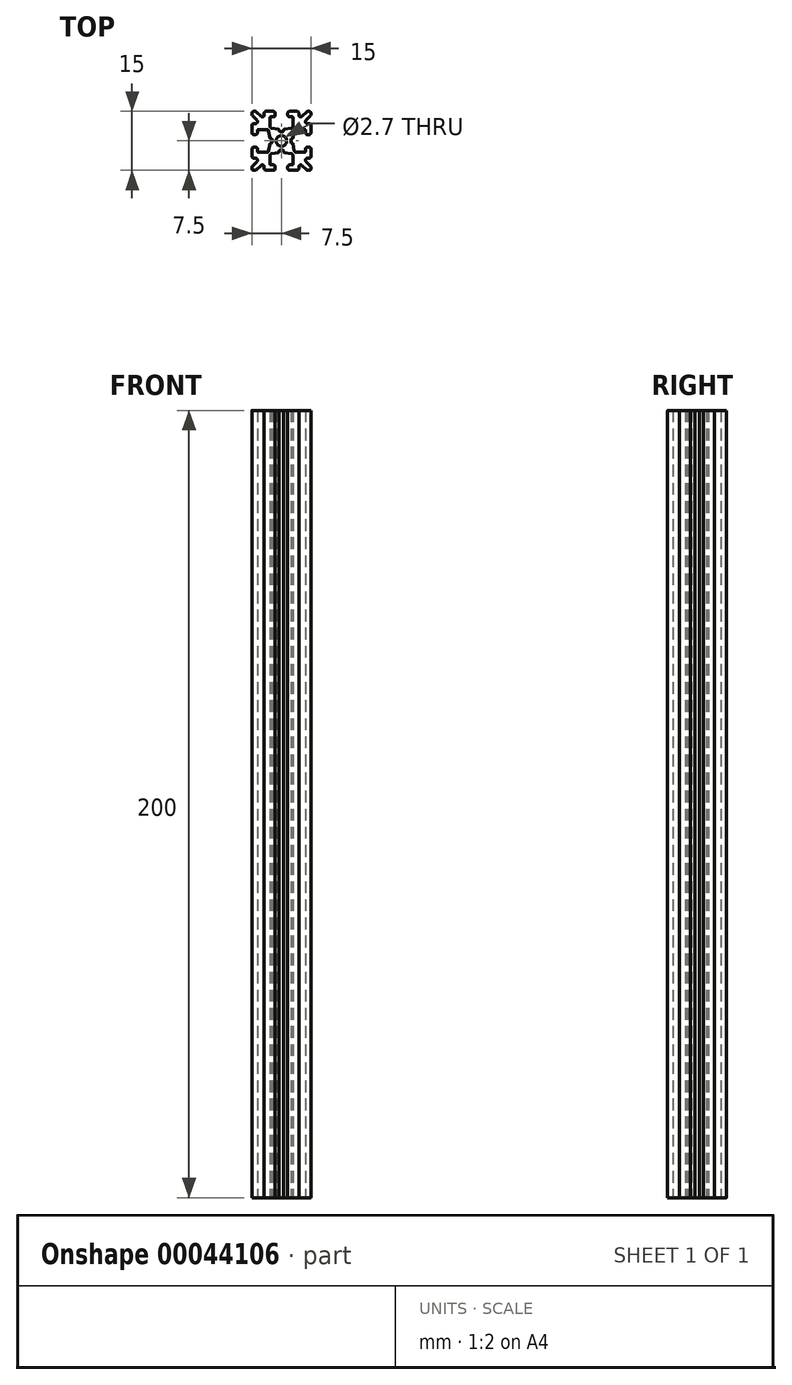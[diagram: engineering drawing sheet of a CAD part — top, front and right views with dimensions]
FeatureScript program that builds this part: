
annotation { "Feature Type Name" : "Feature", "Feature Type Description" : "" }
export const myFeature = defineFeature(function(context is Context, id is Id, definition is map)
    precondition{}
    {
        {
            var Q0;
            Q0=qCreatedBy(makeId("Top.planeOp"),FACE);
            var sketch = newSketch(context, id + "F0", { "sketchPlane" : qUnion([Q0])});
            skLineSegment(sketch, "E0", {"start": v(0, 0) * mm, "end": v(-7.5, -7.5) * mm, "construction": true});
            skArc(sketch, "E1", {"start": v(-1.35, 0) * mm, "mid": v(-1.25, -0.52) * mm, "end": v(-0.95, -0.95) * mm});
            skLineSegment(sketch, "E2", {"start": v(-7.5, -7) * mm, "end": v(-7.5, -6.72) * mm});
            skLineSegment(sketch, "E3", {"start": v(-7.35, -6.36) * mm, "end": v(-6.25, -5.26) * mm});
            skLineSegment(sketch, "E4", {"start": v(-6.6, -4.4) * mm, "end": v(-7, -4.4) * mm});
            skLineSegment(sketch, "E5", {"start": v(-7.5, -3.9) * mm, "end": v(-7.5, -2.1) * mm});
            skLineSegment(sketch, "E6", {"start": v(-7, -1.6) * mm, "end": v(-6.6, -1.6) * mm});
            skLineSegment(sketch, "E7", {"start": v(-6.1, -2.1) * mm, "end": v(-6.1, -2.7) * mm});
            skLineSegment(sketch, "E8", {"start": v(-5.9, -2.9) * mm, "end": v(-3.74, -2.9) * mm});
            skLineSegment(sketch, "E9", {"start": v(-3.25, -2.49) * mm, "end": v(-2.93, -0.73) * mm});
            skLineSegment(sketch, "E10", {"start": v(-2.73, -0.57) * mm, "end": v(-2.6, -0.57) * mm});
            skLineSegment(sketch, "E11", {"start": v(-2.4, -0.37) * mm, "end": v(-2.4, 0) * mm});
            skLineSegment(sketch, "E12", {"start": v(-2.4, 0) * mm, "end": v(-1.35, 0) * mm, "construction": true});
            skPoint(sketch, "E13.visualSharp", {"position": v(-5.4, -4.4) * mm});
            skArc(sketch, "E13.filletArc", {"start": v(-6.25, -5.26) * mm, "mid": v(-6.14, -4.71) * mm, "end": v(-6.6, -4.4) * mm});
            skPoint(sketch, "E14.visualSharp", {"position": v(-6.1, -2.9) * mm});
            skArc(sketch, "E14.filletArc", {"start": v(-6.1, -2.7) * mm, "mid": v(-6.04, -2.84) * mm, "end": v(-5.9, -2.9) * mm});
            skPoint(sketch, "E15.visualSharp", {"position": v(-6.1, -1.6) * mm});
            skArc(sketch, "E15.filletArc", {"start": v(-6.1, -2.1) * mm, "mid": v(-6.25, -1.75) * mm, "end": v(-6.6, -1.6) * mm});
            skPoint(sketch, "E16.visualSharp", {"position": v(-7.5, -1.6) * mm});
            skArc(sketch, "E16.filletArc", {"start": v(-7, -1.6) * mm, "mid": v(-7.35, -1.75) * mm, "end": v(-7.5, -2.1) * mm});
            skPoint(sketch, "E17.visualSharp", {"position": v(-7.5, -4.4) * mm});
            skArc(sketch, "E17.filletArc", {"start": v(-7.5, -3.9) * mm, "mid": v(-7.35, -4.26) * mm, "end": v(-7, -4.4) * mm});
            skPoint(sketch, "E18.visualSharp", {"position": v(-7.5, -6.51) * mm});
            skArc(sketch, "E18.filletArc", {"start": v(-7.35, -6.36) * mm, "mid": v(-7.46, -6.53) * mm, "end": v(-7.5, -6.72) * mm});
            skPoint(sketch, "E19.visualSharp", {"position": v(-3.32, -2.9) * mm});
            skArc(sketch, "E19.filletArc", {"start": v(-3.74, -2.9) * mm, "mid": v(-3.42, -2.78) * mm, "end": v(-3.25, -2.49) * mm});
            skPoint(sketch, "E20.visualSharp", {"position": v(-2.9, -0.57) * mm});
            skArc(sketch, "E20.filletArc", {"start": v(-2.73, -0.57) * mm, "mid": v(-2.86, -0.62) * mm, "end": v(-2.93, -0.73) * mm});
            skPoint(sketch, "E21.visualSharp", {"position": v(-2.4, -0.57) * mm});
            skArc(sketch, "E21.filletArc", {"start": v(-2.6, -0.57) * mm, "mid": v(-2.46, -0.51) * mm, "end": v(-2.4, -0.37) * mm});
            skLineSegment(sketch, "E22.0.MirrorCS", {"start": v(0, -2.4) * mm, "end": v(0, -1.35) * mm, "construction": true});
            skPoint(sketch, "E22.1.MirrorP", {"position": v(-4.4, -7.5) * mm});
            skArc(sketch, "E22.2.MirrorCS", {"start": v(-6.36, -7.35) * mm, "mid": v(-6.53, -7.46) * mm, "end": v(-6.72, -7.5) * mm});
            skPoint(sketch, "E22.3.MirrorP", {"position": v(-1.6, -7.5) * mm});
            skArc(sketch, "E22.4.MirrorCS", {"start": v(-1.6, -7) * mm, "mid": v(-1.75, -7.35) * mm, "end": v(-2.1, -7.5) * mm});
            skArc(sketch, "E22.5.MirrorCS", {"start": v(-0.57, -2.73) * mm, "mid": v(-0.62, -2.86) * mm, "end": v(-0.73, -2.93) * mm});
            skPoint(sketch, "E22.6.MirrorP", {"position": v(-1.6, -6.1) * mm});
            skLineSegment(sketch, "E22.7.MirrorCS", {"start": v(-3.9, -7.5) * mm, "end": v(-2.1, -7.5) * mm});
            skArc(sketch, "E22.8.MirrorCS", {"start": v(-5.26, -6.25) * mm, "mid": v(-4.71, -6.14) * mm, "end": v(-4.4, -6.6) * mm});
            skPoint(sketch, "E22.9.MirrorP", {"position": v(-0.57, -2.4) * mm});
            skPoint(sketch, "E22.10.MirrorP", {"position": v(-4.4, -5.4) * mm});
            skArc(sketch, "E22.11.MirrorCS", {"start": v(-2.7, -6.1) * mm, "mid": v(-2.84, -6.04) * mm, "end": v(-2.9, -5.9) * mm});
            skPoint(sketch, "E22.12.MirrorP", {"position": v(-0.57, -2.9) * mm});
            skLineSegment(sketch, "E22.13.MirrorCS", {"start": v(-7, -7.5) * mm, "end": v(-6.72, -7.5) * mm});
            skLineSegment(sketch, "E22.14.MirrorCS", {"start": v(-1.6, -7) * mm, "end": v(-1.6, -6.6) * mm});
            skLineSegment(sketch, "E22.15.MirrorCS", {"start": v(-6.36, -7.35) * mm, "end": v(-5.26, -6.25) * mm});
            skArc(sketch, "E22.16.MirrorCS", {"start": v(-2.1, -6.1) * mm, "mid": v(-1.75, -6.25) * mm, "end": v(-1.6, -6.6) * mm});
            skLineSegment(sketch, "E22.17.MirrorCS", {"start": v(-4.4, -6.6) * mm, "end": v(-4.4, -7) * mm});
            skArc(sketch, "E22.18.MirrorCS", {"start": v(-2.9, -3.74) * mm, "mid": v(-2.78, -3.42) * mm, "end": v(-2.49, -3.25) * mm});
            skLineSegment(sketch, "E22.19.MirrorCS", {"start": v(-2.9, -5.9) * mm, "end": v(-2.9, -3.74) * mm});
            skLineSegment(sketch, "E22.20.MirrorCS", {"start": v(-2.1, -6.1) * mm, "end": v(-2.7, -6.1) * mm});
            skArc(sketch, "E22.21.MirrorCS", {"start": v(-0.57, -2.6) * mm, "mid": v(-0.51, -2.46) * mm, "end": v(-0.37, -2.4) * mm});
            skLineSegment(sketch, "E22.22.MirrorCS", {"start": v(-0.37, -2.4) * mm, "end": v(0, -2.4) * mm});
            skPoint(sketch, "E22.23.MirrorP", {"position": v(-6.51, -7.5) * mm});
            skPoint(sketch, "E22.24.MirrorP", {"position": v(-2.9, -6.1) * mm});
            skLineSegment(sketch, "E22.25.MirrorCS", {"start": v(-2.49, -3.25) * mm, "end": v(-0.73, -2.93) * mm});
            skLineSegment(sketch, "E22.26.MirrorCS", {"start": v(-0.57, -2.73) * mm, "end": v(-0.57, -2.6) * mm});
            skArc(sketch, "E22.27.MirrorCS", {"start": v(0, -1.35) * mm, "mid": v(-0.52, -1.25) * mm, "end": v(-0.95, -0.95) * mm});
            skArc(sketch, "E22.28.MirrorCS", {"start": v(-3.9, -7.5) * mm, "mid": v(-4.26, -7.35) * mm, "end": v(-4.4, -7) * mm});
            skPoint(sketch, "E22.29.MirrorP", {"position": v(-2.9, -3.32) * mm});
            skPoint(sketch, "E23.visualSharp", {"position": v(-7.5, -7.5) * mm});
            skArc(sketch, "E23.filletArc", {"start": v(-7.5, -7) * mm, "mid": v(-7.35, -7.35) * mm, "end": v(-7, -7.5) * mm});
            skLineSegment(sketch, "E24.0.MirrorCS", {"start": v(0, 2.4) * mm, "end": v(0, 1.35) * mm, "construction": true});
            skLineSegment(sketch, "E24.1.MirrorCS", {"start": v(-2.1, 6.1) * mm, "end": v(-2.7, 6.1) * mm});
            skLineSegment(sketch, "E24.2.MirrorCS", {"start": v(-7.5, 3.9) * mm, "end": v(-7.5, 2.1) * mm});
            skLineSegment(sketch, "E24.3.MirrorCS", {"start": v(-7, 1.6) * mm, "end": v(-6.6, 1.6) * mm});
            skArc(sketch, "E24.4.MirrorCS", {"start": v(-6.1, 2.1) * mm, "mid": v(-6.25, 1.75) * mm, "end": v(-6.6, 1.6) * mm});
            skPoint(sketch, "E24.5.MirrorP", {"position": v(-3.32, 2.9) * mm});
            skPoint(sketch, "E24.6.MirrorP", {"position": v(-0.57, 2.9) * mm});
            skArc(sketch, "E24.7.MirrorCS", {"start": v(-0.57, 2.6) * mm, "mid": v(-0.51, 2.46) * mm, "end": v(-0.37, 2.4) * mm});
            skArc(sketch, "E24.8.MirrorCS", {"start": v(-2.6, 0.57) * mm, "mid": v(-2.46, 0.51) * mm, "end": v(-2.4, 0.37) * mm});
            skLineSegment(sketch, "E24.9.MirrorCS", {"start": v(-0.37, 2.4) * mm, "end": v(0, 2.4) * mm});
            skArc(sketch, "E24.10.MirrorCS", {"start": v(-6.1, 2.7) * mm, "mid": v(-6.04, 2.84) * mm, "end": v(-5.9, 2.9) * mm});
            skPoint(sketch, "E24.11.MirrorP", {"position": v(-4.4, 5.4) * mm});
            skLineSegment(sketch, "E24.12.MirrorCS", {"start": v(-2.9, 5.9) * mm, "end": v(-2.9, 3.74) * mm});
            skLineSegment(sketch, "E24.13.MirrorCS", {"start": v(-7.35, 6.36) * mm, "end": v(-6.25, 5.26) * mm});
            skPoint(sketch, "E24.14.MirrorP", {"position": v(-7.5, 6.51) * mm});
            skArc(sketch, "E24.15.MirrorCS", {"start": v(-3.74, 2.9) * mm, "mid": v(-3.42, 2.78) * mm, "end": v(-3.25, 2.49) * mm});
            skArc(sketch, "E24.16.MirrorCS", {"start": v(-2.1, 6.1) * mm, "mid": v(-1.75, 6.25) * mm, "end": v(-1.6, 6.6) * mm});
            skArc(sketch, "E24.17.MirrorCS", {"start": v(-7, 1.6) * mm, "mid": v(-7.35, 1.75) * mm, "end": v(-7.5, 2.1) * mm});
            skPoint(sketch, "E24.18.MirrorP", {"position": v(-1.6, 6.1) * mm});
            skPoint(sketch, "E24.19.MirrorP", {"position": v(-7.5, 4.4) * mm});
            skLineSegment(sketch, "E24.20.MirrorCS", {"start": v(-4.4, 6.6) * mm, "end": v(-4.4, 7) * mm});
            skArc(sketch, "E24.21.MirrorCS", {"start": v(-7.5, 3.9) * mm, "mid": v(-7.35, 4.26) * mm, "end": v(-7, 4.4) * mm});
            skPoint(sketch, "E24.22.MirrorP", {"position": v(-0.57, 2.4) * mm});
            skLineSegment(sketch, "E24.23.MirrorCS", {"start": v(-5.9, 2.9) * mm, "end": v(-3.74, 2.9) * mm});
            skArc(sketch, "E24.24.MirrorCS", {"start": v(-2.9, 3.74) * mm, "mid": v(-2.78, 3.42) * mm, "end": v(-2.49, 3.25) * mm});
            skArc(sketch, "E24.25.MirrorCS", {"start": v(-7.35, 6.36) * mm, "mid": v(-7.46, 6.53) * mm, "end": v(-7.5, 6.72) * mm});
            skPoint(sketch, "E24.26.MirrorP", {"position": v(-6.1, 2.9) * mm});
            skPoint(sketch, "E24.27.MirrorP", {"position": v(-4.4, 7.5) * mm});
            skArc(sketch, "E24.28.MirrorCS", {"start": v(-5.26, 6.25) * mm, "mid": v(-4.71, 6.14) * mm, "end": v(-4.4, 6.6) * mm});
            skArc(sketch, "E24.29.MirrorCS", {"start": v(-7.5, 7) * mm, "mid": v(-7.35, 7.35) * mm, "end": v(-7, 7.5) * mm});
            skPoint(sketch, "E24.30.MirrorP", {"position": v(-6.1, 1.6) * mm});
            skPoint(sketch, "E24.31.MirrorP", {"position": v(-2.9, 3.32) * mm});
            skPoint(sketch, "E24.32.MirrorP", {"position": v(-1.6, 7.5) * mm});
            skPoint(sketch, "E24.33.MirrorP", {"position": v(-2.9, 6.1) * mm});
            skLineSegment(sketch, "E24.34.MirrorCS", {"start": v(-3.9, 7.5) * mm, "end": v(-2.1, 7.5) * mm});
            skLineSegment(sketch, "E24.35.MirrorCS", {"start": v(-7, 7.5) * mm, "end": v(-6.72, 7.5) * mm});
            skArc(sketch, "E24.36.MirrorCS", {"start": v(-3.9, 7.5) * mm, "mid": v(-4.26, 7.35) * mm, "end": v(-4.4, 7) * mm});
            skPoint(sketch, "E24.37.MirrorP", {"position": v(-7.5, 7.5) * mm});
            skLineSegment(sketch, "E24.38.MirrorCS", {"start": v(-1.6, 7) * mm, "end": v(-1.6, 6.6) * mm});
            skLineSegment(sketch, "E24.39.MirrorCS", {"start": v(-6.36, 7.35) * mm, "end": v(-5.26, 6.25) * mm});
            skPoint(sketch, "E24.40.MirrorP", {"position": v(-7.5, 1.6) * mm});
            skArc(sketch, "E24.41.MirrorCS", {"start": v(-2.7, 6.1) * mm, "mid": v(-2.84, 6.04) * mm, "end": v(-2.9, 5.9) * mm});
            skArc(sketch, "E24.42.MirrorCS", {"start": v(-6.36, 7.35) * mm, "mid": v(-6.53, 7.46) * mm, "end": v(-6.72, 7.5) * mm});
            skLineSegment(sketch, "E24.43.MirrorCS", {"start": v(-2.49, 3.25) * mm, "end": v(-0.73, 2.93) * mm});
            skPoint(sketch, "E24.44.MirrorP", {"position": v(-2.9, 0.57) * mm});
            skLineSegment(sketch, "E24.45.MirrorCS", {"start": v(-6.6, 4.4) * mm, "end": v(-7, 4.4) * mm});
            skArc(sketch, "E24.46.MirrorCS", {"start": v(-1.6, 7) * mm, "mid": v(-1.75, 7.35) * mm, "end": v(-2.1, 7.5) * mm});
            skArc(sketch, "E24.47.MirrorCS", {"start": v(-2.73, 0.57) * mm, "mid": v(-2.86, 0.62) * mm, "end": v(-2.93, 0.73) * mm});
            skArc(sketch, "E24.48.MirrorCS", {"start": v(-6.25, 5.26) * mm, "mid": v(-6.14, 4.71) * mm, "end": v(-6.6, 4.4) * mm});
            skLineSegment(sketch, "E24.49.MirrorCS", {"start": v(-0.57, 2.73) * mm, "end": v(-0.57, 2.6) * mm});
            skLineSegment(sketch, "E24.50.MirrorCS", {"start": v(-2.73, 0.57) * mm, "end": v(-2.6, 0.57) * mm});
            skArc(sketch, "E24.51.MirrorCS", {"start": v(-1.35, 0) * mm, "mid": v(-1.25, 0.52) * mm, "end": v(-0.95, 0.95) * mm});
            skPoint(sketch, "E24.52.MirrorP", {"position": v(-2.4, 0.57) * mm});
            skPoint(sketch, "E24.53.MirrorP", {"position": v(-5.4, 4.4) * mm});
            skLineSegment(sketch, "E24.54.MirrorCS", {"start": v(-2.4, 0.37) * mm, "end": v(-2.4, 0) * mm});
            skArc(sketch, "E24.55.MirrorCS", {"start": v(0, 1.35) * mm, "mid": v(-0.52, 1.25) * mm, "end": v(-0.95, 0.95) * mm});
            skLineSegment(sketch, "E24.56.MirrorCS", {"start": v(-3.25, 2.49) * mm, "end": v(-2.93, 0.73) * mm});
            skLineSegment(sketch, "E24.57.MirrorCS", {"start": v(-6.1, 2.1) * mm, "end": v(-6.1, 2.7) * mm});
            skLineSegment(sketch, "E24.58.MirrorCS", {"start": v(-7.5, 7) * mm, "end": v(-7.5, 6.72) * mm});
            skArc(sketch, "E24.59.MirrorCS", {"start": v(-0.57, 2.73) * mm, "mid": v(-0.62, 2.86) * mm, "end": v(-0.73, 2.93) * mm});
            skPoint(sketch, "E24.60.MirrorP", {"position": v(-6.51, 7.5) * mm});
            skLineSegment(sketch, "E25.0.MirrorCS", {"start": v(7, -7.5) * mm, "end": v(6.72, -7.5) * mm});
            skLineSegment(sketch, "E25.1.MirrorCS", {"start": v(0.57, 2.73) * mm, "end": v(0.57, 2.6) * mm});
            skLineSegment(sketch, "E25.2.MirrorCS", {"start": v(0.37, 2.4) * mm, "end": v(0, 2.4) * mm});
            skLineSegment(sketch, "E25.3.MirrorCS", {"start": v(7, 7.5) * mm, "end": v(6.72, 7.5) * mm});
            skLineSegment(sketch, "E25.4.MirrorCS", {"start": v(1.6, -7) * mm, "end": v(1.6, -6.6) * mm});
            skLineSegment(sketch, "E25.5.MirrorCS", {"start": v(2.73, 0.57) * mm, "end": v(2.6, 0.57) * mm});
            skLineSegment(sketch, "E25.6.MirrorCS", {"start": v(7, 1.6) * mm, "end": v(6.6, 1.6) * mm});
            skLineSegment(sketch, "E25.7.MirrorCS", {"start": v(5.9, 2.9) * mm, "end": v(3.74, 2.9) * mm});
            skLineSegment(sketch, "E25.8.MirrorCS", {"start": v(7.35, 6.36) * mm, "end": v(6.25, 5.26) * mm});
            skArc(sketch, "E25.9.MirrorCS", {"start": v(2.7, -6.1) * mm, "mid": v(2.84, -6.04) * mm, "end": v(2.9, -5.9) * mm});
            skArc(sketch, "E25.10.MirrorCS", {"start": v(2.9, 3.74) * mm, "mid": v(2.78, 3.42) * mm, "end": v(2.49, 3.25) * mm});
            skPoint(sketch, "E25.11.MirrorP", {"position": v(1.6, -7.5) * mm});
            skPoint(sketch, "E25.12.MirrorP", {"position": v(6.1, -1.6) * mm});
            skPoint(sketch, "E25.13.MirrorP", {"position": v(2.9, 3.32) * mm});
            skPoint(sketch, "E25.14.MirrorP", {"position": v(7.5, -1.6) * mm});
            skArc(sketch, "E25.15.MirrorCS", {"start": v(1.6, 7) * mm, "mid": v(1.75, 7.35) * mm, "end": v(2.1, 7.5) * mm});
            skLineSegment(sketch, "E25.16.MirrorCS", {"start": v(6.1, -2.1) * mm, "end": v(6.1, -2.7) * mm});
            skLineSegment(sketch, "E25.17.MirrorCS", {"start": v(2.4, 0.37) * mm, "end": v(2.4, 0) * mm});
            skArc(sketch, "E25.18.MirrorCS", {"start": v(7, -1.6) * mm, "mid": v(7.35, -1.75) * mm, "end": v(7.5, -2.1) * mm});
            skArc(sketch, "E25.19.MirrorCS", {"start": v(7.5, 7) * mm, "mid": v(7.35, 7.35) * mm, "end": v(7, 7.5) * mm});
            skArc(sketch, "E25.20.MirrorCS", {"start": v(2.1, -6.1) * mm, "mid": v(1.75, -6.25) * mm, "end": v(1.6, -6.6) * mm});
            skArc(sketch, "E25.21.MirrorCS", {"start": v(6.1, 2.1) * mm, "mid": v(6.25, 1.75) * mm, "end": v(6.6, 1.6) * mm});
            skLineSegment(sketch, "E25.22.MirrorCS", {"start": v(4.4, 6.6) * mm, "end": v(4.4, 7) * mm});
            skLineSegment(sketch, "E25.23.MirrorCS", {"start": v(6.6, 4.4) * mm, "end": v(7, 4.4) * mm});
            skArc(sketch, "E25.24.MirrorCS", {"start": v(7, 1.6) * mm, "mid": v(7.35, 1.75) * mm, "end": v(7.5, 2.1) * mm});
            skArc(sketch, "E25.25.MirrorCS", {"start": v(0, -1.35) * mm, "mid": v(0.52, -1.25) * mm, "end": v(0.95, -0.95) * mm});
            skLineSegment(sketch, "E25.26.MirrorCS", {"start": v(3.9, -7.5) * mm, "end": v(2.1, -7.5) * mm});
            skLineSegment(sketch, "E25.27.MirrorCS", {"start": v(2.1, 6.1) * mm, "end": v(2.7, 6.1) * mm});
            skLineSegment(sketch, "E25.28.MirrorCS", {"start": v(2.73, -0.57) * mm, "end": v(2.6, -0.57) * mm});
            skLineSegment(sketch, "E25.29.MirrorCS", {"start": v(4.4, -6.6) * mm, "end": v(4.4, -7) * mm});
            skLineSegment(sketch, "E25.30.MirrorCS", {"start": v(3.9, 7.5) * mm, "end": v(2.1, 7.5) * mm});
            skArc(sketch, "E25.31.MirrorCS", {"start": v(0.57, -2.73) * mm, "mid": v(0.62, -2.86) * mm, "end": v(0.73, -2.93) * mm});
            skArc(sketch, "E25.32.MirrorCS", {"start": v(0.57, 2.6) * mm, "mid": v(0.51, 2.46) * mm, "end": v(0.37, 2.4) * mm});
            skPoint(sketch, "E25.33.MirrorP", {"position": v(6.51, -7.5) * mm});
            skArc(sketch, "E25.34.MirrorCS", {"start": v(3.9, -7.5) * mm, "mid": v(4.26, -7.35) * mm, "end": v(4.4, -7) * mm});
            skArc(sketch, "E25.35.MirrorCS", {"start": v(2.7, 6.1) * mm, "mid": v(2.84, 6.04) * mm, "end": v(2.9, 5.9) * mm});
            skPoint(sketch, "E25.36.MirrorP", {"position": v(0.57, -2.4) * mm});
            skPoint(sketch, "E25.37.MirrorP", {"position": v(0.57, 2.9) * mm});
            skLineSegment(sketch, "E25.38.MirrorCS", {"start": v(3.25, -2.49) * mm, "end": v(2.93, -0.73) * mm});
            skPoint(sketch, "E25.39.MirrorP", {"position": v(5.4, -4.4) * mm});
            skPoint(sketch, "E25.40.MirrorP", {"position": v(2.4, -0.57) * mm});
            skLineSegment(sketch, "E25.41.MirrorCS", {"start": v(7.5, -7) * mm, "end": v(7.5, -6.72) * mm});
            skArc(sketch, "E25.42.MirrorCS", {"start": v(7.35, 6.36) * mm, "mid": v(7.46, 6.53) * mm, "end": v(7.5, 6.72) * mm});
            skPoint(sketch, "E25.43.MirrorP", {"position": v(4.4, 7.5) * mm});
            skArc(sketch, "E25.44.MirrorCS", {"start": v(6.25, 5.26) * mm, "mid": v(6.14, 4.71) * mm, "end": v(6.6, 4.4) * mm});
            skPoint(sketch, "E25.45.MirrorP", {"position": v(6.1, -2.9) * mm});
            skPoint(sketch, "E25.46.MirrorP", {"position": v(4.4, -7.5) * mm});
            skArc(sketch, "E25.47.MirrorCS", {"start": v(6.1, 2.7) * mm, "mid": v(6.04, 2.84) * mm, "end": v(5.9, 2.9) * mm});
            skLineSegment(sketch, "E25.48.MirrorCS", {"start": v(2.1, -6.1) * mm, "end": v(2.7, -6.1) * mm});
            skArc(sketch, "E25.49.MirrorCS", {"start": v(2.73, -0.57) * mm, "mid": v(2.86, -0.62) * mm, "end": v(2.93, -0.73) * mm});
            skArc(sketch, "E25.50.MirrorCS", {"start": v(7.35, -6.36) * mm, "mid": v(7.46, -6.53) * mm, "end": v(7.5, -6.72) * mm});
            skLineSegment(sketch, "E25.51.MirrorCS", {"start": v(3.25, 2.49) * mm, "end": v(2.93, 0.73) * mm});
            skArc(sketch, "E25.52.MirrorCS", {"start": v(2.9, -3.74) * mm, "mid": v(2.78, -3.42) * mm, "end": v(2.49, -3.25) * mm});
            skArc(sketch, "E25.53.MirrorCS", {"start": v(2.6, 0.57) * mm, "mid": v(2.46, 0.51) * mm, "end": v(2.4, 0.37) * mm});
            skPoint(sketch, "E25.54.MirrorP", {"position": v(2.9, 0.57) * mm});
            skPoint(sketch, "E25.55.MirrorP", {"position": v(7.5, -6.51) * mm});
            skLineSegment(sketch, "E25.56.MirrorCS", {"start": v(2.49, 3.25) * mm, "end": v(0.73, 2.93) * mm});
            skArc(sketch, "E25.57.MirrorCS", {"start": v(1.6, -7) * mm, "mid": v(1.75, -7.35) * mm, "end": v(2.1, -7.5) * mm});
            skArc(sketch, "E25.58.MirrorCS", {"start": v(2.1, 6.1) * mm, "mid": v(1.75, 6.25) * mm, "end": v(1.6, 6.6) * mm});
            skLineSegment(sketch, "E25.59.MirrorCS", {"start": v(0.57, -2.73) * mm, "end": v(0.57, -2.6) * mm});
            skLineSegment(sketch, "E25.60.MirrorCS", {"start": v(2.4, -0.37) * mm, "end": v(2.4, 0) * mm});
            skArc(sketch, "E25.61.MirrorCS", {"start": v(7.5, -3.9) * mm, "mid": v(7.35, -4.26) * mm, "end": v(7, -4.4) * mm});
            skLineSegment(sketch, "E25.62.MirrorCS", {"start": v(5.9, -2.9) * mm, "end": v(3.74, -2.9) * mm});
            skLineSegment(sketch, "E25.63.MirrorCS", {"start": v(7.5, -3.9) * mm, "end": v(7.5, -2.1) * mm});
            skLineSegment(sketch, "E25.64.MirrorCS", {"start": v(7, -1.6) * mm, "end": v(6.6, -1.6) * mm});
            skArc(sketch, "E25.65.MirrorCS", {"start": v(1.35, 0) * mm, "mid": v(1.25, -0.52) * mm, "end": v(0.95, -0.95) * mm});
            skPoint(sketch, "E25.66.MirrorP", {"position": v(7.5, 1.6) * mm});
            skPoint(sketch, "E25.67.MirrorP", {"position": v(1.6, 6.1) * mm});
            skLineSegment(sketch, "E25.68.MirrorCS", {"start": v(6.36, -7.35) * mm, "end": v(5.26, -6.25) * mm});
            skPoint(sketch, "E25.69.MirrorP", {"position": v(2.4, 0.57) * mm});
            skPoint(sketch, "E25.70.MirrorP", {"position": v(6.1, 1.6) * mm});
            skPoint(sketch, "E25.71.MirrorP", {"position": v(3.32, -2.9) * mm});
            skPoint(sketch, "E25.72.MirrorP", {"position": v(0.57, -2.9) * mm});
            skPoint(sketch, "E25.73.MirrorP", {"position": v(7.5, 4.4) * mm});
            skArc(sketch, "E25.74.MirrorCS", {"start": v(5.26, -6.25) * mm, "mid": v(4.71, -6.14) * mm, "end": v(4.4, -6.6) * mm});
            skArc(sketch, "E25.75.MirrorCS", {"start": v(7.5, -7) * mm, "mid": v(7.35, -7.35) * mm, "end": v(7, -7.5) * mm});
            skLineSegment(sketch, "E25.76.MirrorCS", {"start": v(2.49, -3.25) * mm, "end": v(0.73, -2.93) * mm});
            skArc(sketch, "E25.77.MirrorCS", {"start": v(3.74, 2.9) * mm, "mid": v(3.42, 2.78) * mm, "end": v(3.25, 2.49) * mm});
            skArc(sketch, "E25.78.MirrorCS", {"start": v(6.36, -7.35) * mm, "mid": v(6.53, -7.46) * mm, "end": v(6.72, -7.5) * mm});
            skArc(sketch, "E25.79.MirrorCS", {"start": v(7.5, 3.9) * mm, "mid": v(7.35, 4.26) * mm, "end": v(7, 4.4) * mm});
            skArc(sketch, "E25.80.MirrorCS", {"start": v(2.73, 0.57) * mm, "mid": v(2.86, 0.62) * mm, "end": v(2.93, 0.73) * mm});
            skArc(sketch, "E25.81.MirrorCS", {"start": v(6.36, 7.35) * mm, "mid": v(6.53, 7.46) * mm, "end": v(6.72, 7.5) * mm});
            skPoint(sketch, "E25.82.MirrorP", {"position": v(4.4, -5.4) * mm});
            skPoint(sketch, "E25.83.MirrorP", {"position": v(6.51, 7.5) * mm});
            skPoint(sketch, "E25.84.MirrorP", {"position": v(2.9, -0.57) * mm});
            skLineSegment(sketch, "E25.85.MirrorCS", {"start": v(2.9, -5.9) * mm, "end": v(2.9, -3.74) * mm});
            skLineSegment(sketch, "E25.86.MirrorCS", {"start": v(6.1, 2.1) * mm, "end": v(6.1, 2.7) * mm});
            skLineSegment(sketch, "E25.87.MirrorCS", {"start": v(6.36, 7.35) * mm, "end": v(5.26, 6.25) * mm});
            skArc(sketch, "E25.88.MirrorCS", {"start": v(0.57, 2.73) * mm, "mid": v(0.62, 2.86) * mm, "end": v(0.73, 2.93) * mm});
            skArc(sketch, "E25.89.MirrorCS", {"start": v(0.57, -2.6) * mm, "mid": v(0.51, -2.46) * mm, "end": v(0.37, -2.4) * mm});
            skLineSegment(sketch, "E25.90.MirrorCS", {"start": v(2.9, 5.9) * mm, "end": v(2.9, 3.74) * mm});
            skArc(sketch, "E25.91.MirrorCS", {"start": v(0, 1.35) * mm, "mid": v(0.52, 1.25) * mm, "end": v(0.95, 0.95) * mm});
            skArc(sketch, "E25.92.MirrorCS", {"start": v(2.6, -0.57) * mm, "mid": v(2.46, -0.51) * mm, "end": v(2.4, -0.37) * mm});
            skPoint(sketch, "E25.93.MirrorP", {"position": v(4.4, 5.4) * mm});
            skPoint(sketch, "E25.94.MirrorP", {"position": v(2.9, -3.32) * mm});
            skPoint(sketch, "E25.95.MirrorP", {"position": v(2.9, 6.1) * mm});
            skPoint(sketch, "E25.96.MirrorP", {"position": v(5.4, 4.4) * mm});
            skPoint(sketch, "E25.97.MirrorP", {"position": v(3.32, 2.9) * mm});
            skArc(sketch, "E25.98.MirrorCS", {"start": v(3.74, -2.9) * mm, "mid": v(3.42, -2.78) * mm, "end": v(3.25, -2.49) * mm});
            skArc(sketch, "E25.99.MirrorCS", {"start": v(3.9, 7.5) * mm, "mid": v(4.26, 7.35) * mm, "end": v(4.4, 7) * mm});
            skPoint(sketch, "E25.100.MirrorP", {"position": v(7.5, -4.4) * mm});
            skPoint(sketch, "E25.101.MirrorP", {"position": v(6.1, 2.9) * mm});
            skArc(sketch, "E25.102.MirrorCS", {"start": v(1.35, 0) * mm, "mid": v(1.25, 0.52) * mm, "end": v(0.95, 0.95) * mm});
            skArc(sketch, "E25.103.MirrorCS", {"start": v(5.26, 6.25) * mm, "mid": v(4.71, 6.14) * mm, "end": v(4.4, 6.6) * mm});
            skPoint(sketch, "E25.104.MirrorP", {"position": v(7.5, 6.51) * mm});
            skPoint(sketch, "E25.105.MirrorP", {"position": v(2.9, -6.1) * mm});
            skArc(sketch, "E25.106.MirrorCS", {"start": v(6.25, -5.26) * mm, "mid": v(6.14, -4.71) * mm, "end": v(6.6, -4.4) * mm});
            skArc(sketch, "E25.107.MirrorCS", {"start": v(6.1, -2.1) * mm, "mid": v(6.25, -1.75) * mm, "end": v(6.6, -1.6) * mm});
            skPoint(sketch, "E25.108.MirrorP", {"position": v(1.6, 7.5) * mm});
            skPoint(sketch, "E25.109.MirrorP", {"position": v(7.5, 7.5) * mm});
            skLineSegment(sketch, "E25.110.MirrorCS", {"start": v(0.37, -2.4) * mm, "end": v(0, -2.4) * mm});
            skPoint(sketch, "E25.111.MirrorP", {"position": v(7.5, -7.5) * mm});
            skLineSegment(sketch, "E25.112.MirrorCS", {"start": v(7.5, 7) * mm, "end": v(7.5, 6.72) * mm});
            skArc(sketch, "E25.113.MirrorCS", {"start": v(6.1, -2.7) * mm, "mid": v(6.04, -2.84) * mm, "end": v(5.9, -2.9) * mm});
            skLineSegment(sketch, "E25.114.MirrorCS", {"start": v(1.6, 7) * mm, "end": v(1.6, 6.6) * mm});
            skPoint(sketch, "E25.115.MirrorP", {"position": v(1.6, -6.1) * mm});
            skLineSegment(sketch, "E25.116.MirrorCS", {"start": v(7.35, -6.36) * mm, "end": v(6.25, -5.26) * mm});
            skLineSegment(sketch, "E25.117.MirrorCS", {"start": v(7.5, 3.9) * mm, "end": v(7.5, 2.1) * mm});
            skPoint(sketch, "E25.118.MirrorP", {"position": v(0.57, 2.4) * mm});
            skLineSegment(sketch, "E25.119.MirrorCS", {"start": v(6.6, -4.4) * mm, "end": v(7, -4.4) * mm});
            skSolve(sketch);
        }
        {
            var Q0;
            Q0=makeQuery(id+"F0.imprint","IMPRINT",FACE,{"disambiguationData":[TD([[makeQuery(id+"F0.imprint","IMPRINT",EDGE,{"derivedFrom":sQuery(id+"F0.wireOp",EDGE,"E1")}),-1.0]])]});
            extrude(context, id + "F1", {"entities" : qUnion([Q0]), "depth" : 200 * mm});
        }
    });
